# Revit family: PRD_FrankeWS_WCSqttngPns_CAMPUSSquatPan_HDTX504
name_source: partatom
category: Plumbing Fixtures
revit_build: Autodesk Revit 2018 (Build: 20190510_1515(x64)
units: mm (PartAtom-declared; Revit-internal decimal feet)

## family parameters
Cut with Voids When Loaded = Yes
Host = Face
OmniClass Number = 23.45.05.21.11.21
OmniClass Title = Urinals
Part Type = Normal
Room Calculation Point = No
Round Connector Dimension = Use Diameter
Shared = Yes

## types (1)
- HDTX504
    AssetType = Fixed
    BIMObjectName = PRD_AR_WCSquattingPans_CAMPUSSquatPan_HDTX504
    Category = Pr_40_20_93_96, WC squatting pans
    Default Elevation = 1100 mm
    Description = Squat pan made of stainless steel, suitable for DN 20 in-wall flush valves, surface satin finished, material thickness 1 mm, 9 liter flushing capacity, with circular folded edge (22 mm), circular flushing rim, suicide-resistant. Vertical connection from behind with screw connection of 28 mm diameter, internal DN 100 waste outlet, fixing material and height adjustment included.
    DiameterNominal = 100  [stored 0.328084 ft]
    DurationUnit = year
    Features = stainless steel, surface satin finished, material thickness 1 mm, 9 liter flushing capacity
    Finish = Satin finished
    GeneralMaterial = PRD_AR_StainlessSteel_SatinFinished
    GrossWeight = 16.00 kg
    IfcExportAs = IfcSanitaryTerminalType
    IfcExportType = URINAL
    IntakeSize = 28  [stored 0.0918635 ft]
    IntegralAccessories = fixing material and height adjustment included
    Manufacturer = KWC Group AG
    ManufacturerName = KWC Group AG
    ManufacturerURL = www.kwc.com
    Material = Stainless steel
    MaterialCode = 1.4301 Chrome Nickel steel V2A
    MaterialThickness = 1.00 mm
    Model = HDTX504
    ModelNumber = 2000108804
    ModelReference = HDTX504
    Mounting = Pedestal
    Name = CAMPUS Squat pan HDTX504
    NetWeight = 14.50 kg
    NominalDepth = 755 mm  [stored 2.47703 ft]
    NominalHeight = 200 mm  [stored 0.656168 ft]
    NominalWidth = 755 mm  [stored 2.47703 ft]
    OutletSize = DN 100
    ProductInformation = https://pim.kwc.com
    Size = 755 x 200 x 755 mm (W x H x D)
    SpilloverLevel = 0 mm  [stored 0 ft]
    TailorMade = No
    TypeOfMounting = Inset floor mounting
    TypeOfToiletSeat = No seat
    TypeOfWC = Squat-pan
    URL = www.kwc.com
    Uniclass2015Code = Pr_40_20_93_96
    Uniclass2015Title = WC squatting pans
    Uniclass2015Version = Products v1.23
    UrinalType = Stall
    Version = 1
    WarrantyDurationUnit = year

note: [stored X ft] marks values corroborated as IEEE doubles in the binary element streams (Revit-internal decimal feet)

## geometry (parser evidence)
native form markers: Sweep x5
no freeform markers — native parametric forms only
